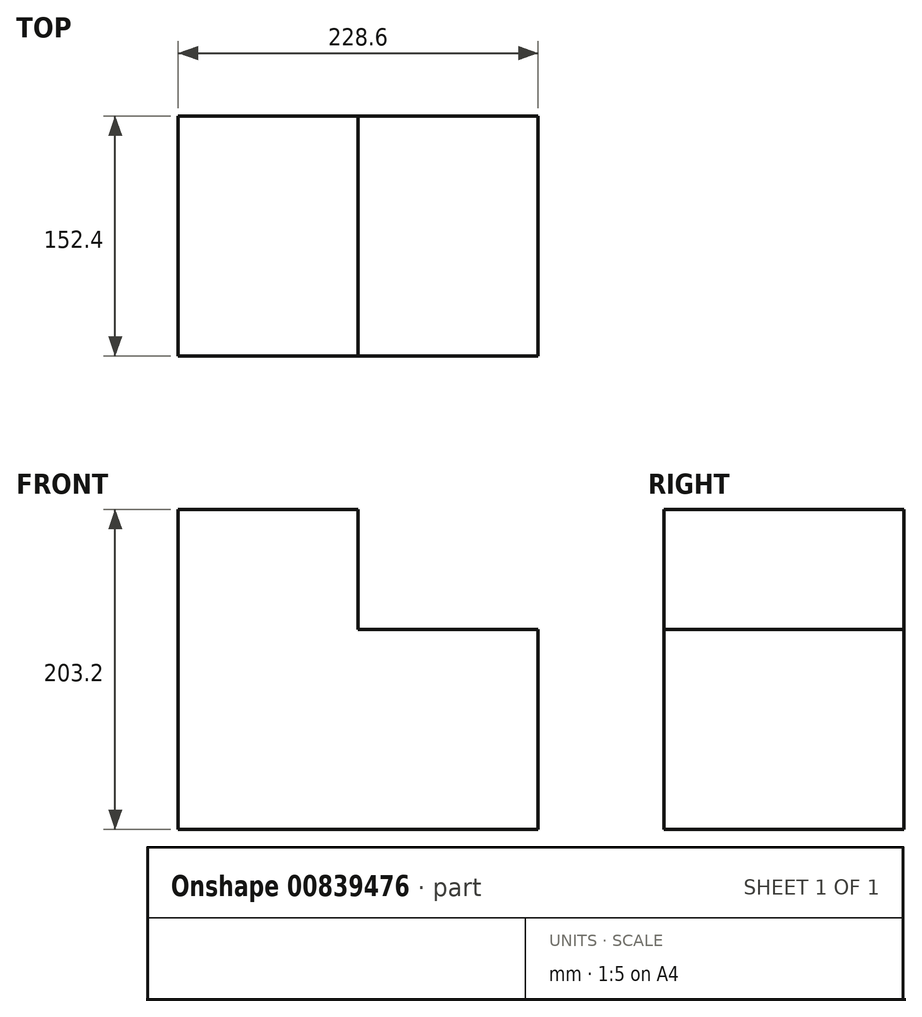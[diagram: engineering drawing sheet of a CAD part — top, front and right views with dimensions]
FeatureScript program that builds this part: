
annotation { "Feature Type Name" : "Feature", "Feature Type Description" : "" }
export const myFeature = defineFeature(function(context is Context, id is Id, definition is map)
    precondition{}
    {
        {
            var Q0;
            Q0=qCreatedBy(makeId("Front.planeOp"),FACE);
            var sketch = newSketch(context, id + "F0", { "sketchPlane" : qUnion([Q0])});
            skLineSegment(sketch, "E0.bottom", {"start": v(-107.46, 75.22) * mm, "end": v(121.14, 75.22) * mm});
            skLineSegment(sketch, "E0.top", {"start": v(-107.46, -51.78) * mm, "end": v(121.14, -51.78) * mm});
            skLineSegment(sketch, "E0.left", {"start": v(-107.46, 75.22) * mm, "end": v(-107.46, -51.78) * mm});
            skLineSegment(sketch, "E0.right", {"start": v(121.14, 75.22) * mm, "end": v(121.14, -51.78) * mm});
            skSolve(sketch);
        }
        {
            var Q0;
            Q0 = qSketchRegion(id + "F0", true);
            extrude(context, id + "F1", {"entities" : qUnion([Q0]), "depth" : 152.4 * mm, "offsetDistance" : 25.4 * mm});
        }
        {
            var Q0;
            Q0=makeQuery(id+"F1.opExtrude","SWEPT_FACE",FACE,{"disambiguationData":[OSD([sQuery(id+"F0.wireOp",EDGE,"E0.bottom")])]});
            var sketch = newSketch(context, id + "F2", { "sketchPlane" : qUnion([Q0])});
            skLineSegment(sketch, "E1.bottom", {"start": v(-107.46, -152.4) * mm, "end": v(6.84, -152.4) * mm});
            skLineSegment(sketch, "E1.top", {"start": v(-107.46, 0) * mm, "end": v(6.84, 0) * mm});
            skLineSegment(sketch, "E1.left", {"start": v(-107.46, -152.4) * mm, "end": v(-107.46, 0) * mm});
            skLineSegment(sketch, "E1.right", {"start": v(6.84, -152.4) * mm, "end": v(6.84, 0) * mm});
            skSolve(sketch);
        }
        {
            var Q0;
            Q0 = qSketchRegion(id + "F2", true);
            extrude(context, id + "F3", {"entities" : qUnion([Q0]), "operationType" : NewBodyOperationType.ADD, "depth" : 76.2 * mm, "offsetDistance" : 25.4 * mm});
        }
    });
